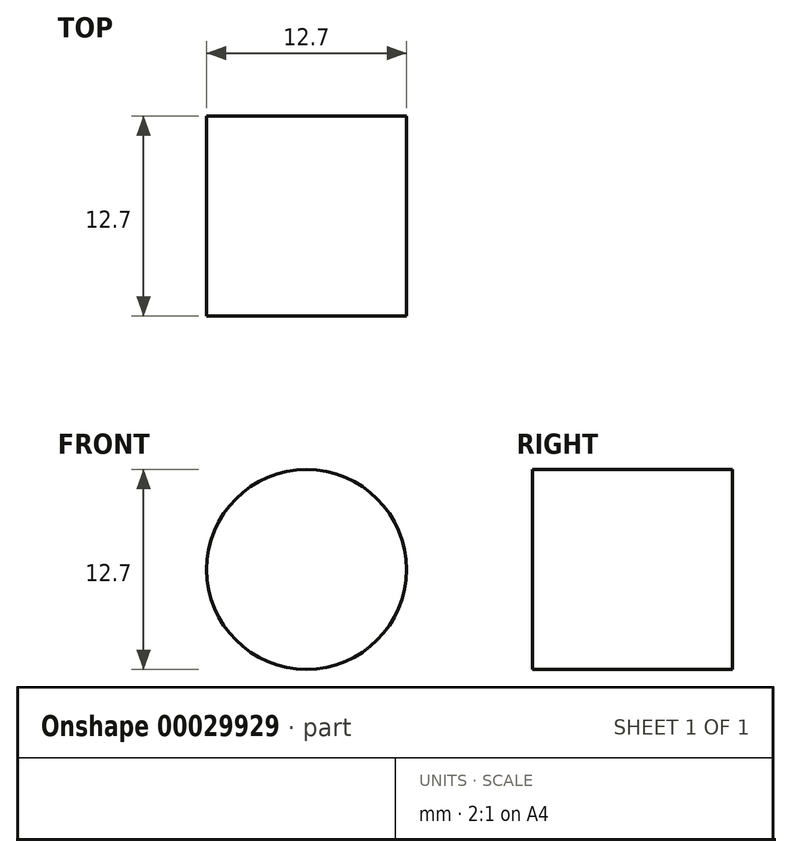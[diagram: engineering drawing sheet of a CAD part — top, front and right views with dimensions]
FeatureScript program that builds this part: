
annotation { "Feature Type Name" : "Feature", "Feature Type Description" : "" }
export const myFeature = defineFeature(function(context is Context, id is Id, definition is map)
    precondition{}
    {
        {
            var Q0;
            Q0=qCreatedBy(makeId("Front.planeOp"),FACE);
            var sketch = newSketch(context, id + "F0", { "sketchPlane" : qUnion([Q0])});
            skCircle(sketch, "E0", {"center": v(0, 0) * mm, "radius": 6.35 * mm});
            skSolve(sketch);
        }
        {
            var Q0;
            Q0=makeQuery(id+"F0.imprint","IMPRINT",FACE,{"disambiguationData":[TD([[makeQuery(id+"F0.imprint","IMPRINT",EDGE,{"derivedFrom":sQuery(id+"F0.wireOp",EDGE,"E0")}),1.0]])]});
            extrude(context, id + "F1", {"entities" : qUnion([Q0]), "depth" : 12.7 * mm});
        }
    });
